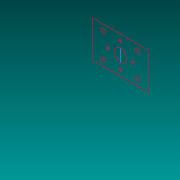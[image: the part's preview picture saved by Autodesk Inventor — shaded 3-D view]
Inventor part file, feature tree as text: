
AUTODESK INVENTOR PART (.ipt)
format: ipt  version: 2013 SP2 (Build 170200200, 200)  size: 295,936 bytes
history: native  units: mm
features: sheet_metal_op x15, sketch x11, other x9, chamfer x8, plane x1, mirror x1
ambient origin geometry x8: Origin, YZ Plane, XZ Plane, XY Plane, X Axis, Y Axis, Z Axis, Center Point
bodies: Solid1 (feature_tree)
feature tree (45):
  sheet_metal_op  "Face1"
  sheet_metal_op  "Flange3"
  sheet_metal_op  "Flange4"
  sketch  "Sketch6"  dims[d23=2.0mm]
  sheet_metal_op  "Face2"
  sketch  "Sketch7"  dims[d24=1.0mm]
  plane  "Work Plane1"
  mirror  "Mirror1"
  chamfer  "Corner Round1"
  sketch  "Sketch9"  dims[d26=2.0mm]
  sketch  "Sketch10"  dims[d27=50.0mm d28=90.0deg d29=2.0mm]
  sheet_metal_op  "Flange5"
  sheet_metal_op  "Flange6"
  chamfer  "Corner Round7"
  chamfer  "Corner Round8"
  chamfer  "Corner Round9"
  chamfer  "Corner Round10"
  chamfer  "Corner Round11"
  chamfer  "Corner Round12"
  chamfer  "Corner Round13"
  sketch  "Sketch1"  dims[d0=36.0mm]
  other  "Plate1"
  sketch  "Sketch4"  dims[d1=27.5mm]
  other  "Plate4"
  sheet_metal_op  "Bend3"
  sheet_metal_op  "Corner3"
  sketch  "Sketch5"  dims[d2=2.0mm]
  other  "Plate5"
  sheet_metal_op  "Bend4"
  sheet_metal_op  "Corner4"
  other  "Plate6"
  sheet_metal_op  "Bend5"
  sketch  "Sketch8"  dims[d25=4.0mm]
  sketch  "Sketch11"  dims[d30=8.0mm]
  sketch  "Sketch12"  dims[d31=2.0mm]
  other  "Plate7"
  sheet_metal_op  "Bend6"
  sheet_metal_op  "Corner5"
  sketch  "Sketch13"  dims[d32=2.0mm d33=2.0mm d34=1.0mm d35=4.0mm d36=2.0mm d37=50.0mm d38=90.0deg d39=2.0mm d40=8.0mm d41=2.0mm d42=2.0mm d46=2.0mm d47=2.0mm d48=1.0mm d49=4.0mm d50=2.0mm d51=2.0mm d52=0.0mm d53=90.0deg d54=2.0mm d55=0.0mm d56=6.0mm d62=16.0mm d63=22.0mm d64=3.0mm d65=3.0mm d66=3.0mm d67=3.0mm d68=2.0mm d69=0.0mm d70=2.0mm d71=1.0mm d72=4.0mm d73=2.0mm d74=5.0mm d75=90.0deg d76=2.0mm d77=8.0mm d78=2.0mm d79=2.0mm d80=2.0mm d81=1.0mm d82=4.0mm d83=2.0mm d84=5.0mm d85=90.0deg d86=2.0mm d87=8.0mm d88=2.0mm d89=2.0mm d90=6.0mm d91=6.0mm d92=6.0mm d93=6.0mm d94=6.0mm d95=6.0mm d96=6.0mm]
  other  "Plate8"
  sheet_metal_op  "Bend7"
  sheet_metal_op  "Corner6"
  other  "Cut1"
  other  "Cut2"
  other  "Cut3"
